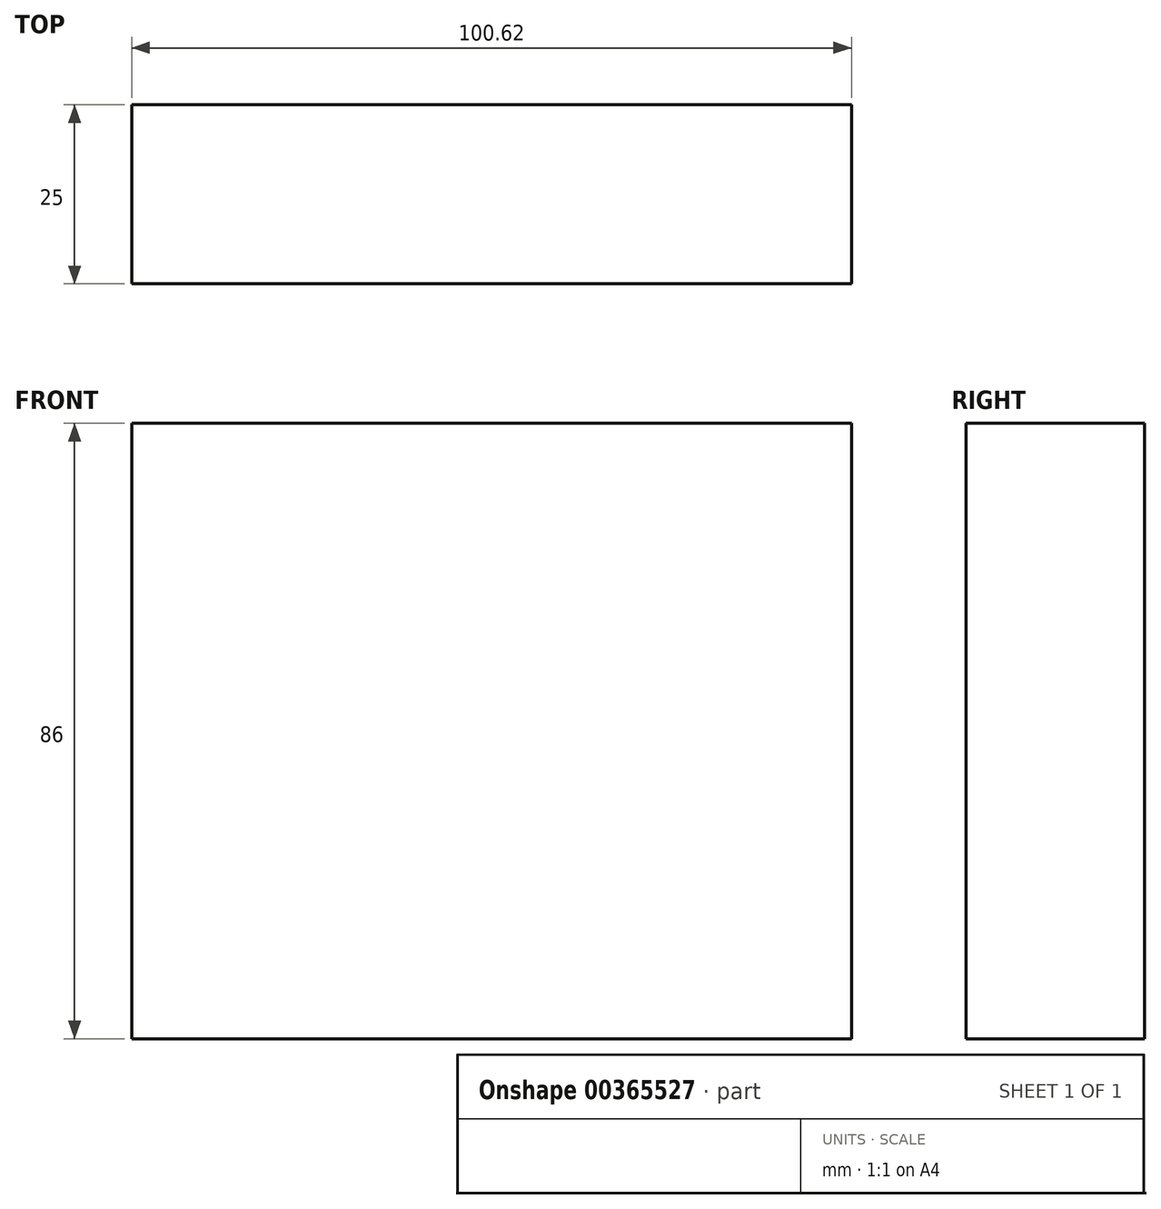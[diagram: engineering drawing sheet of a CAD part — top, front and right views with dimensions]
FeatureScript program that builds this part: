
annotation { "Feature Type Name" : "Feature", "Feature Type Description" : "" }
export const myFeature = defineFeature(function(context is Context, id is Id, definition is map)
    precondition{}
    {
        {
            var Q0;
            Q0=qCreatedBy(makeId("Front.planeOp"),FACE);
            var sketch = newSketch(context, id + "F0", { "sketchPlane" : qUnion([Q0])});
            skLineSegment(sketch, "E0.bottom", {"start": v(50.31, -43) * mm, "end": v(-50.31, -43) * mm});
            skLineSegment(sketch, "E0.top", {"start": v(50.31, 43) * mm, "end": v(-50.31, 43) * mm});
            skLineSegment(sketch, "E0.left", {"start": v(50.31, -43) * mm, "end": v(50.31, 43) * mm});
            skLineSegment(sketch, "E0.right", {"start": v(-50.31, -43) * mm, "end": v(-50.31, 43) * mm});
            skPoint(sketch, "E0.middle", {"position": v(0, 0) * mm});
            skSolve(sketch);
        }
        {
            var Q0;
            Q0=makeQuery(id+"F0.imprint","IMPRINT",FACE,{"disambiguationData":[TD([[makeQuery(id+"F0.imprint","IMPRINT",EDGE,{"derivedFrom":sQuery(id+"F0.wireOp",EDGE,"E0.bottom")}),-1.0]])]});
            extrude(context, id + "F1", {"entities" : qUnion([Q0]), "depth" : 25 * mm});
        }
    });
